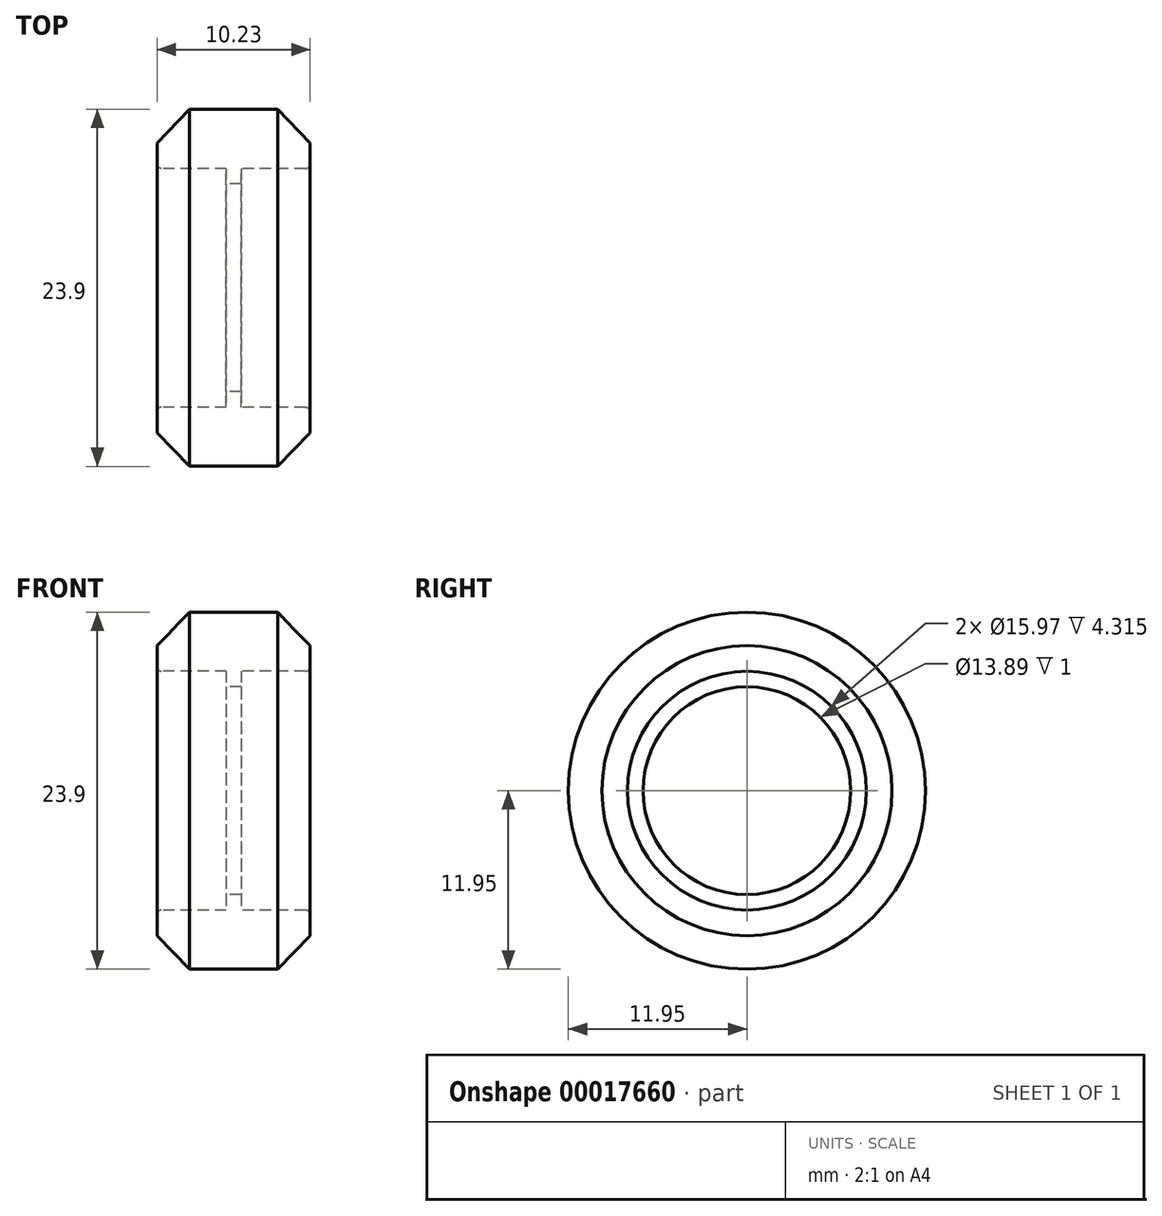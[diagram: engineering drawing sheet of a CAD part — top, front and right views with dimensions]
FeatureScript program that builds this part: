
annotation { "Feature Type Name" : "Feature", "Feature Type Description" : "" }
export const myFeature = defineFeature(function(context is Context, id is Id, definition is map)
    precondition{}
    {
        {
            var Q0;
            Q0=qCreatedBy(makeId("Front.planeOp"),FACE);
            var sketch = newSketch(context, id + "F0", { "sketchPlane" : qUnion([Q0])});
            skLineSegment(sketch, "E0", {"start": v(0, 7.99) * mm, "end": v(0, 9.7) * mm});
            skLineSegment(sketch, "E1", {"start": v(2.17, 11.95) * mm, "end": v(0, 9.7) * mm});
            skLineSegment(sketch, "E2", {"start": v(2.17, 11.95) * mm, "end": v(8.06, 11.95) * mm});
            skLineSegment(sketch, "E3", {"start": v(10.23, 9.7) * mm, "end": v(8.06, 11.95) * mm});
            skLineSegment(sketch, "E4", {"start": v(10.23, 9.7) * mm, "end": v(10.23, 7.99) * mm});
            skLineSegment(sketch, "E5", {"start": v(10.23, 7.99) * mm, "end": v(5.62, 7.99) * mm});
            skLineSegment(sketch, "E6", {"start": v(5.62, 7.99) * mm, "end": v(5.62, 6.95) * mm});
            skLineSegment(sketch, "E7", {"start": v(5.62, 6.95) * mm, "end": v(4.62, 6.95) * mm});
            skLineSegment(sketch, "E8", {"start": v(4.62, 6.95) * mm, "end": v(4.62, 7.99) * mm});
            skLineSegment(sketch, "E9", {"start": v(4.62, 7.99) * mm, "end": v(0, 7.99) * mm});
            skLineSegment(sketch, "E10", {"start": v(1.57, 0) * mm, "end": v(7.84, 0) * mm, "construction": true});
            skSolve(sketch);
        }
        {
            var Q0;
            Q0=makeQuery(id+"F0.imprint","IMPRINT",FACE,{"disambiguationData":[TD([[makeQuery(id+"F0.imprint","IMPRINT",EDGE,{"derivedFrom":sQuery(id+"F0.wireOp",EDGE,"E0")}),-1.0]])]});
            var Q1;
            Q1=sQuery(id+"F0.wireOp",EDGE,"E10");
            revolve(context, id + "F1", {"entities" : qUnion([Q0]), "axis" : qUnion([Q1]), "revolveType" : RevolveType.FULL});
        }
        {
            var Q0;
            Q0=makeQuery(id+"F1.opRevolve","SWEPT_EDGE",EDGE,{"disambiguationData":[OSD([sQuery(id+"F0.wireOp",EDGE,"E4"),sQuery(id+"F0.wireOp",EDGE,"E5")])]});
            var Q1;
            Q1=makeQuery(id+"F1.opRevolve","SWEPT_EDGE",EDGE,{"disambiguationData":[OSD([sQuery(id+"F0.wireOp",EDGE,"E0"),sQuery(id+"F0.wireOp",EDGE,"E9")])]});
            fillet(context, id + "F2", {"entities" : qUnion([Q0, Q1]), "radius" : 0.3 * mm, "allowEdgeOverflow" : false});
        }
    });
